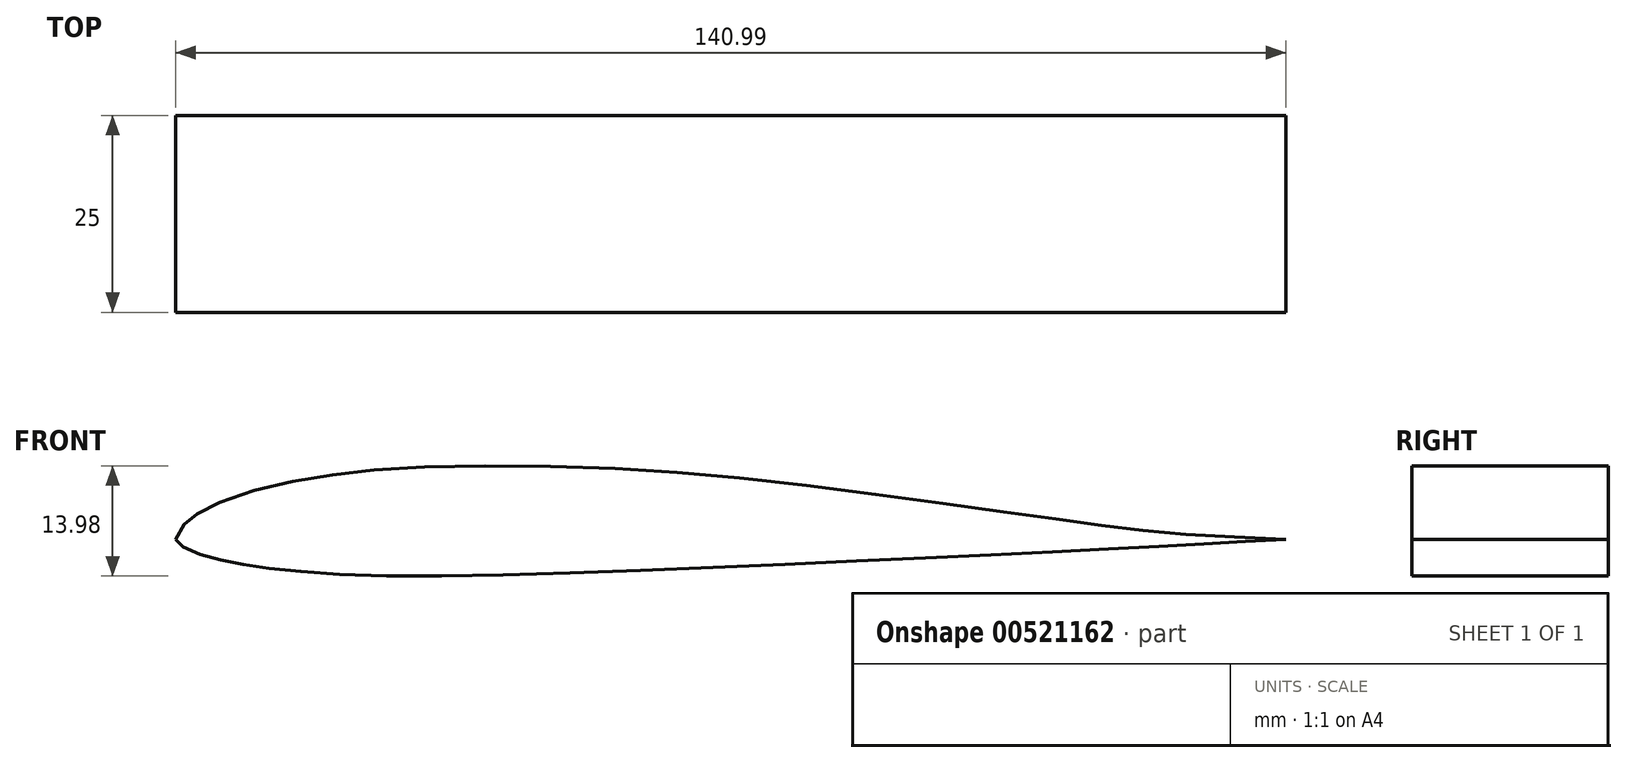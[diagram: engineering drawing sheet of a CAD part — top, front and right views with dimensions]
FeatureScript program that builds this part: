
annotation { "Feature Type Name" : "Feature", "Feature Type Description" : "" }
export const myFeature = defineFeature(function(context is Context, id is Id, definition is map)
    precondition{}
    {
        {
            var Q0;
            Q0=qCreatedBy(makeId("Front.planeOp"),FACE);
            var sketch = newSketch(context, id + "F0", { "sketchPlane" : qUnion([Q0])});
            skFitSpline(sketch, "E0", {"points": [v(0, 0) * mm, v(0.72, 1.56) * mm, v(1.9, 2.63) * mm, v(3.57, 3.74) * mm, v(9.37, 6.05) * mm, v(18.32, 7.96) * mm, v(29.46, 9.1) * mm, v(52.07, 9.15) * mm, v(74.9, 7.44) * mm, v(101.27, 4.03) * mm, v(116.74, 1.9) * mm, v(126.91, 0.76) * mm, v(141, 0) * mm], "startDerivative": vector(0, 48.95) * mm, "endDerivative": vector(151.48, -6.38) * mm});
            skLineSegment(sketch, "E1", {"start": v(0, 0) * mm, "end": v(0, 13.62) * mm, "construction": true});
            skFitSpline(sketch, "E2", {"points": [v(0, 0) * mm, v(0.74, -0.86) * mm, v(4.52, -2.32) * mm, v(10.37, -3.47) * mm, v(25.45, -4.59) * mm, v(72.79, -3.36) * mm, v(119.6, -1.17) * mm, v(141, 0) * mm], "startDerivative": vector(0, -20.22) * mm, "endDerivative": vector(116.28, 6.64) * mm});
            skSolve(sketch);
        }
        {
            var Q0;
            Q0=makeQuery(id+"F0.imprint","IMPRINT",FACE,{"disambiguationData":[TD([[makeQuery(id+"F0.imprint","IMPRINT",EDGE,{"derivedFrom":sQuery(id+"F0.wireOp",EDGE,"E0")}),-1.0]])]});
            extrude(context, id + "F1", {"entities" : qUnion([Q0]), "depth" : 25 * mm, "offsetDistance" : 25 * mm});
        }
    });
